annotation { "Feature Type Name" : "Feature", "Feature Type Description" : "" }
export const myFeature = defineFeature(function(context is Context, id is Id, definition is map)
    precondition{}
    {
        {
            var Q0;
            Q0=qCreatedBy(makeId("Right.planeOp"),FACE);
            var sketch = newSketch(context, id + "F0", { "sketchPlane" : qUnion([Q0])});
            skCircle(sketch, "E0.cCircle", {"center": v(0, 0) * mm, "radius": 4.5 * mm, "construction": true});
            skLineSegment(sketch, "E0.0", {"start": v(2.6, -4.5) * mm, "end": v(-2.6, -4.5) * mm});
            skLineSegment(sketch, "E0.1", {"start": v(-2.6, -4.5) * mm, "end": v(-5.2, 0) * mm});
            skLineSegment(sketch, "E0.2", {"start": v(-5.2, 0) * mm, "end": v(-2.6, 4.5) * mm});
            skLineSegment(sketch, "E0.3", {"start": v(-2.6, 4.5) * mm, "end": v(2.6, 4.5) * mm});
            skLineSegment(sketch, "E0.4", {"start": v(2.6, 4.5) * mm, "end": v(5.2, 0) * mm});
            skLineSegment(sketch, "E0.5", {"start": v(5.2, 0) * mm, "end": v(2.6, -4.5) * mm});
            skPoint(sketch, "E0.0.midPoint", {"position": v(0, -4.5) * mm});
            skSolve(sketch);
        }
        {
            var Q0;
            Q0=qCreatedBy(makeId("Right.planeOp"),FACE);
            var sketch = newSketch(context, id + "F1", { "sketchPlane" : qUnion([Q0])});
            skCircle(sketch, "E1.cCircle", {"center": v(0, 0) * mm, "radius": 4 * mm, "construction": true});
            skLineSegment(sketch, "E1.0", {"start": v(2.3, -4) * mm, "end": v(-2.3, -4) * mm});
            skLineSegment(sketch, "E1.1", {"start": v(-2.3, -4) * mm, "end": v(-4.62, 0) * mm});
            skLineSegment(sketch, "E1.2", {"start": v(-4.62, 0) * mm, "end": v(-2.3, 4) * mm});
            skLineSegment(sketch, "E1.3", {"start": v(-2.3, 4) * mm, "end": v(2.3, 4) * mm});
            skLineSegment(sketch, "E1.4", {"start": v(2.3, 4) * mm, "end": v(4.62, 0) * mm});
            skLineSegment(sketch, "E1.5", {"start": v(4.62, 0) * mm, "end": v(2.3, -4) * mm});
            skPoint(sketch, "E1.0.midPoint", {"position": v(0, -4) * mm});
            skSolve(sketch);
        }
        {
            var Q0;
            Q0 = qSketchRegion(id + "F0", true);
            extrude(context, id + "F2", {"entities" : qUnion([Q0]), "depth" : 150 * mm, "offsetDistance" : 25.4 * mm});
        }
        {
            var Q0;
            Q0 = qSketchRegion(id + "F1", true);
            extrude(context, id + "F3", {"entities" : qUnion([Q0]), "operationType" : NewBodyOperationType.REMOVE, "depth" : 150 * mm, "offsetDistance" : 25.4 * mm});
        }
        {
            var Q0;
            Q0=qCreatedBy(makeId("Top.planeOp"),FACE);
            cPlane(context, id + "F4", {"entities" : qUnion([Q0]), "cplaneType" : CPlaneType.OFFSET, "offset" : 4.5 * mm, "width" : 152.4 * mm, "height" : 152.4 * mm});
        }
        {
            var Q0;
            Q0=qCreatedBy(id+"F4.planeOp",FACE);
            var sketch = newSketch(context, id + "F5", { "sketchPlane" : qUnion([Q0])});
            skText(sketch, "E2", { "text": "Ali Rashid", "fontName": "RobotoSlab-Bold.ttf"});
            const initialGuessF5  = {"E2": [0.01524, -0.00787, 1, 0, 0.01588]};
            skSetInitialGuess(sketch, initialGuessF5);
            skSolve(sketch);
        }
        {
            var Q0;
            Q0 = qSketchRegion(id + "F5", true);
            extrude(context, id + "F6", {"entities" : qUnion([Q0]), "operationType" : NewBodyOperationType.ADD, "depth" : 1 * mm, "offsetDistance" : 25.4 * mm});
        }
        {
            var Q0;
            Q0=qCreatedBy(id+"F4.planeOp",FACE);
            var sketch = newSketch(context, id + "F7", { "sketchPlane" : qUnion([Q0])});
            skLineSegment(sketch, "E3.bottom", {"start": v(39.53, 9.79) * mm, "end": v(43.94, 9.79) * mm});
            skLineSegment(sketch, "E3.top", {"start": v(39.53, 2.58) * mm, "end": v(43.94, 2.58) * mm});
            skLineSegment(sketch, "E3.left", {"start": v(39.53, 9.79) * mm, "end": v(39.53, 2.58) * mm});
            skLineSegment(sketch, "E3.right", {"start": v(43.94, 9.79) * mm, "end": v(43.94, 2.58) * mm});
            skLineSegment(sketch, "E4.bottom", {"start": v(104.79, 9.79) * mm, "end": v(109.2, 9.79) * mm});
            skLineSegment(sketch, "E4.top", {"start": v(104.79, 2.58) * mm, "end": v(109.2, 2.58) * mm});
            skLineSegment(sketch, "E4.left", {"start": v(104.79, 9.79) * mm, "end": v(104.79, 2.58) * mm});
            skLineSegment(sketch, "E4.right", {"start": v(109.2, 9.79) * mm, "end": v(109.2, 2.58) * mm});
            skSolve(sketch);
        }
        {
            var Q0;
            Q0 = qSketchRegion(id + "F7", true);
            extrude(context, id + "F8", {"entities" : qUnion([Q0]), "depth" : 0.5 * mm, "offsetDistance" : 25.4 * mm});
        }
    });